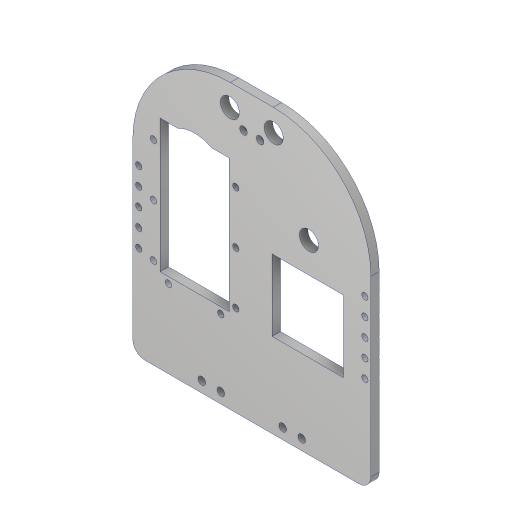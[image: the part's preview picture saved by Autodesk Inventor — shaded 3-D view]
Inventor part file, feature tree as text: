
AUTODESK INVENTOR PART (.ipt)
format: ipt  version: 2023.2 (Build 272271000, 271)  size: 367,616 bytes
history: native  units: mm
features: extrude x15, sketch x15, chamfer x4, fillet x2, other x1
ambient origin geometry x8: Origin, YZ Plane, XZ Plane, XY Plane, X Axis, Y Axis, Z Axis, Center Point
bodies: Body1 (feature_tree)
feature tree (37):
  other  "솔리드1"
  extrude  "돌출1"  Depth=100.02mm
  extrude  "돌출2"  Depth=50.01mm
  extrude  "돌출3"  Depth=94.0mm
  extrude  "돌출4"  Depth=40.0mm
  extrude  "돌출5"  Depth=3.5mm TaperAngle=0.0deg
  extrude  "돌출6"  Depth=28.0mm
  chamfer  "모따기2"  Distance=24.01mm
  extrude  "돌출7"  Depth=53.1mm
  fillet  "모깎기1"  Radius=4.0mm
  extrude  "돌출8"  Depth=10.4mm
  chamfer  "모따기3"  Distance=55.9mm
  extrude  "돌출9"  Depth=29.04mm
  chamfer  "모따기4"  Distance=14.52mm
  extrude  "돌출10"  Depth=4.0mm TaperAngle=0.0deg
  extrude  "돌출11"  Depth=30.0mm
  fillet  "모깎기2"  Radius=4.0mm
  extrude  "돌출13"  Depth=3.41mm
  chamfer  "모따기6"  Distance=2.7mm
  extrude  "돌출17"  Depth=2.7mm
  extrude  "돌출15"  Depth=2.7mm
  extrude  "돌출16"  Depth=2.7mm
  sketch  "스케치1"
  sketch  "스케치2"
  sketch  "스케치3"
  sketch  "스케치4"
  sketch  "스케치5"
  sketch  "스케치6"
  sketch  "스케치7"
  sketch  "스케치8"
  sketch  "스케치9"
  sketch  "스케치10"
  sketch  "스케치11"
  sketch  "스케치13"
  sketch  "스케치15"
  sketch  "스케치16"
  sketch  "스케치17"
